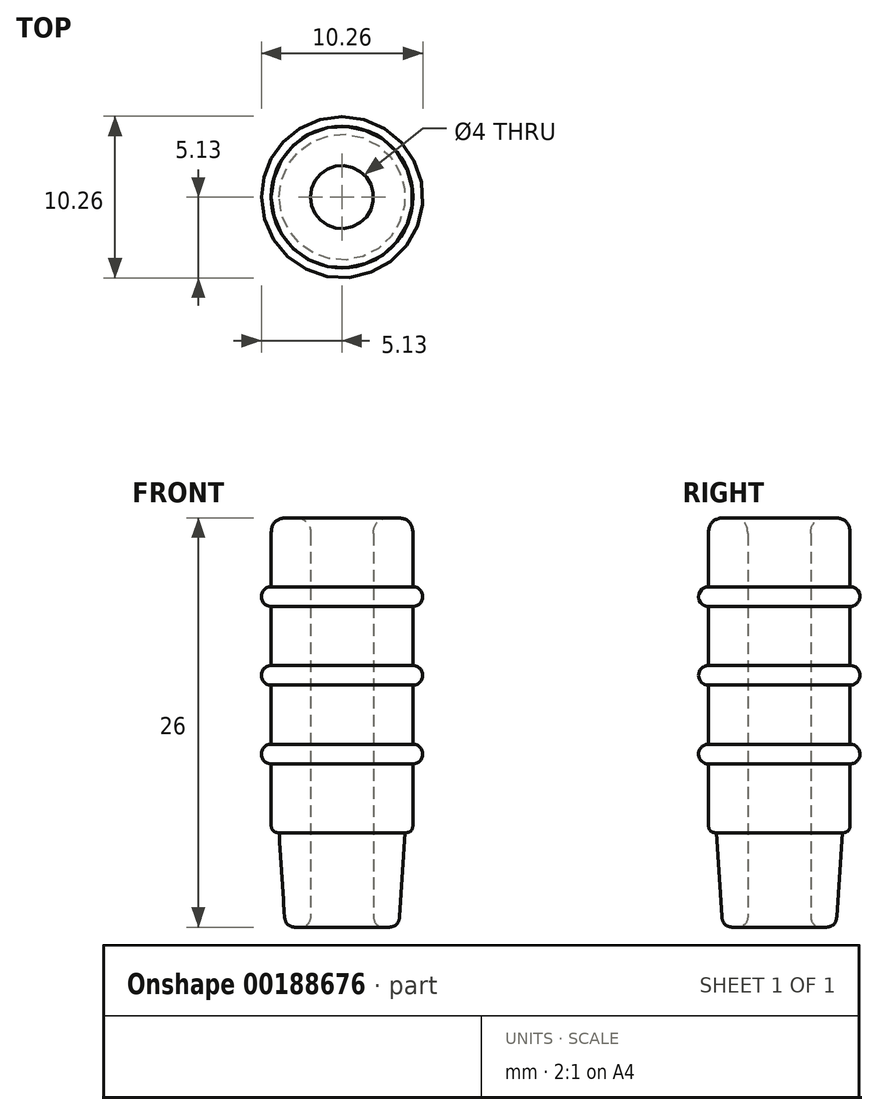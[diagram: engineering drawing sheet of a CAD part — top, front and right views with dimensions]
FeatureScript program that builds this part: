
annotation { "Feature Type Name" : "Feature", "Feature Type Description" : "" }
export const myFeature = defineFeature(function(context is Context, id is Id, definition is map)
    precondition{}
    {
        {
            var Q0;
            Q0=qCreatedBy(makeId("Top.planeOp"),FACE);
            var sketch = newSketch(context, id + "F0", { "sketchPlane" : qUnion([Q0])});
            skCircle(sketch, "E0", {"center": v(0, 0) * mm, "radius": 2 * mm});
            skCircle(sketch, "E1", {"center": v(0, 0) * mm, "radius": 3.6 * mm});
            skSolve(sketch);
        }
        {
            var Q0;
            Q0=makeQuery(id+"F0.imprint","IMPRINT",FACE,{"disambiguationData":[TD([[makeQuery(id+"F0.imprint","IMPRINT",EDGE,{"derivedFrom":sQuery(id+"F0.wireOp",EDGE,"E0")}),-1.0]])]});
            cPlane(context, id + "F1", {"entities" : qUnion([Q0]), "cplaneType" : CPlaneType.OFFSET, "offset" : 6 * mm, "width" : 150 * mm, "height" : 150 * mm});
        }
        {
            var Q0;
            Q0=qCreatedBy(makeId("Front.planeOp"),FACE);
            var sketch = newSketch(context, id + "F2", { "sketchPlane" : qUnion([Q0])});
            skLineSegment(sketch, "E2", {"start": v(0, 0) * mm, "end": v(2, 0) * mm});
            skLineSegment(sketch, "E3", {"start": v(2, 0) * mm, "end": v(3.61, 0) * mm});
            skLineSegment(sketch, "E4", {"start": v(0, 0) * mm, "end": v(0, 6) * mm});
            skLineSegment(sketch, "E5", {"start": v(0, 6) * mm, "end": v(2, 6) * mm});
            skLineSegment(sketch, "E6", {"start": v(2, 6) * mm, "end": v(4, 6) * mm});
            skLineSegment(sketch, "E7", {"start": v(4, 6) * mm, "end": v(3.61, 0) * mm});
            skLineSegment(sketch, "E8", {"start": v(2, 6) * mm, "end": v(2, 0) * mm});
            skLineSegment(sketch, "E9", {"start": v(0, 6) * mm, "end": v(0, -2.73) * mm});
            skSolve(sketch);
        }
        {
            var Q0;
            Q0=makeQuery(id+"F2.imprint","IMPRINT",FACE,{"disambiguationData":[TD([[makeQuery(id+"F2.imprint","IMPRINT",EDGE,{"derivedFrom":sQuery(id+"F2.wireOp",EDGE,"E3")}),1.0]])]});
            var Q1;
            Q1=sQuery(id+"F2.wireOp",EDGE,"E4");
            revolve(context, id + "F3", {"entities" : qUnion([Q0]), "axis" : qUnion([Q1]), "revolveType" : RevolveType.FULL});
        }
        {
            var Q0;
            Q0=qCreatedBy(makeId("Front.planeOp"),FACE);
            var sketch = newSketch(context, id + "F4", { "sketchPlane" : qUnion([Q0])});
            skLineSegment(sketch, "E10", {"start": v(0, 0) * mm, "end": v(0, 6) * mm});
            skLineSegment(sketch, "E11", {"start": v(0, 6) * mm, "end": v(0, 26) * mm});
            skLineSegment(sketch, "E12", {"start": v(0, 26) * mm, "end": v(2, 26) * mm});
            skLineSegment(sketch, "E13", {"start": v(2, 26) * mm, "end": v(4.5, 26) * mm});
            skLineSegment(sketch, "E14", {"start": v(2, 26) * mm, "end": v(2, 6) * mm});
            skLineSegment(sketch, "E15", {"start": v(2, 6) * mm, "end": v(4.5, 6) * mm});
            skLineSegment(sketch, "E16", {"start": v(4.5, 26) * mm, "end": v(4.5, 21.63) * mm});
            skLineSegment(sketch, "E17", {"start": v(4.5, 20.38) * mm, "end": v(4.5, 16.62) * mm});
            skLineSegment(sketch, "E18", {"start": v(4.5, 15.38) * mm, "end": v(4.5, 11.62) * mm});
            skArc(sketch, "E19", {"start": v(4.5, 20.38) * mm, "mid": v(5.12, 21) * mm, "end": v(4.5, 21.63) * mm});
            skArc(sketch, "E20", {"start": v(4.5, 15.38) * mm, "mid": v(5.12, 16) * mm, "end": v(4.5, 16.62) * mm});
            skArc(sketch, "E21", {"start": v(4.5, 10.37) * mm, "mid": v(5.12, 11) * mm, "end": v(4.5, 11.62) * mm});
            skLineSegment(sketch, "E22.trimOffspring", {"start": v(4.5, 10.37) * mm, "end": v(4.5, 6) * mm});
            skSolve(sketch);
        }
        {
            var Q0;
            Q0=makeQuery(id+"F4.imprint","IMPRINT",FACE,{"disambiguationData":[TD([[makeQuery(id+"F4.imprint","IMPRINT",EDGE,{"derivedFrom":sQuery(id+"F4.wireOp",EDGE,"E13")}),-1.0]])]});
            var Q1;
            Q1=sQuery(id+"F4.wireOp",EDGE,"E11");
            revolve(context, id + "F5", {"operationType" : NewBodyOperationType.ADD, "entities" : qUnion([Q0]), "axis" : qUnion([Q1]), "revolveType" : RevolveType.FULL});
        }
        {
            var Q0;
            Q0=makeQuery(id+"F3.opRevolve","SWEPT_EDGE",EDGE,{"disambiguationData":[OSD([sQuery(id+"F2.wireOp",EDGE,"E2"),sQuery(id+"F2.wireOp",EDGE,"E3"),sQuery(id+"F2.wireOp",EDGE,"E8")])]});
            var Q1;
            Q1=makeQuery(id+"F3.opRevolve","SWEPT_EDGE",EDGE,{"disambiguationData":[OSD([sQuery(id+"F2.wireOp",EDGE,"E3"),sQuery(id+"F2.wireOp",EDGE,"E7")])]});
            fillet(context, id + "F6", {"entities" : qUnion([Q0, Q1]), "radius" : .75 * mm, "tangentPropagation" : true, "rho" : 0.5, "crossSection" : FilletCrossSection.CONIC, "allowEdgeOverflow" : false});
        }
        {
            var Q0;
            Q0=makeQuery(id+"F5.opRevolve","SWEPT_EDGE",EDGE,{"disambiguationData":[OSD([sQuery(id+"F4.wireOp",EDGE,"E15"),sQuery(id+"F4.wireOp",EDGE,"E22.trimOffspring")])]});
            fillet(context, id + "F7", {"entities" : qUnion([Q0]), "radius" : .5 * mm, "tangentPropagation" : true, "rho" : 0.5, "crossSection" : FilletCrossSection.CONIC, "allowEdgeOverflow" : false});
        }
        {
            var Q0;
            Q0=makeQuery(id+"F5.opRevolve","SWEPT_EDGE",EDGE,{"disambiguationData":[OSD([sQuery(id+"F4.wireOp",EDGE,"E13"),sQuery(id+"F4.wireOp",EDGE,"E16")])]});
            var Q1;
            Q1=makeQuery(id+"F5.opRevolve","SWEPT_EDGE",EDGE,{"disambiguationData":[OSD([sQuery(id+"F4.wireOp",EDGE,"E13"),sQuery(id+"F4.wireOp",EDGE,"E14")])]});
            fillet(context, id + "F8", {"entities" : qUnion([Q0, Q1]), "radius" : 1 * mm, "tangentPropagation" : true, "rho" : 0.5, "crossSection" : FilletCrossSection.CONIC, "allowEdgeOverflow" : false});
        }
    });
